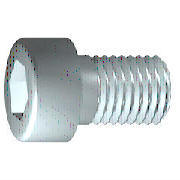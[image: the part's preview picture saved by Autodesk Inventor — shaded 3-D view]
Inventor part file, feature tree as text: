
AUTODESK INVENTOR PART (.ipt)
format: ipt  version: 2018 (Build 220112000, 112)  size: 196,608 bytes
history: native  units: mm (DEFAULTED — no unit token found)
features: sketch x2, extrude x1, plane x1, fillet x1
ambient origin geometry x7: Origin, YZ Plane, XY Plane, X Axis, Y Axis, Z Axis, Center Point
bodies: Solid1 (feature_tree), Body (feature_tree)
feature tree (5):
  extrude  "Slot"  Depth=6.0mm
  plane  "Work Plane1"
  fillet  "Fillet2"  Radius=6.0mm
  sketch  "Sketch1"  dims[d1=9.5mm d2=0.61355mm d3=6.0mm]
  sketch  "Sketch2"  dims[d4=3.0mm d5=60.0deg d6=6.0mm d7=6.0mm d8=5.773503mm d9=10.0mm d10=90.0deg d11=10.0mm d12=0.0mm d13=9.5mm d14=0.0mm d15=0.61345mm d16=0.61345mm d17=0.6mm d19=0.0mm d26=12.0mm d27=45.0deg d28=0.0mm d29=0.0mm d30=0.1mm]
